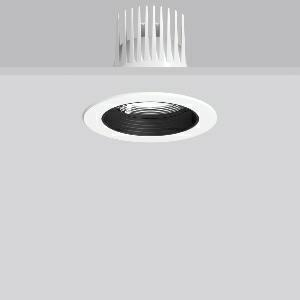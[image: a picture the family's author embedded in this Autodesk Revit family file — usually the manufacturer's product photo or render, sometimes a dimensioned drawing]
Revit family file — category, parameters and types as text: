
# Revit family: heledon_maxi_e_901767_002_2_c0ee
name_source: partatom
category: Lighting Fixtures
units: mm (PartAtom-declared; Revit-internal decimal feet)

## family parameters
Cut with Voids When Loaded = No
Host = Face
Light Source = No
Part Type = Normal
Room Calculation Point = No
Round Connector Dimension = Use Diameter
Shared = No

## types (1)
- HELEDON maxi E (1 x LED Modul 927, 3500 lm, 2700)
    Apparent Load = 35 VA
    Approval mark = CE
    CIE Flux Codes = 97 100 100 100 100
    Color Rendering = 92
    Color Temperature = 2700
    Default Elevation = 1800 mm
    Description = Series: HELEDON maxi
Round recessed downlight. Housing: die-cast aluminium, powder-coated. Black plastic ring and recessed LED to prevent glare from the side. Optical assembly with lens made of plastic (polycarbonate) for the best homogeneous light distribution - can be changed without tools. Best colour rendering index Ra>90. Suitable for Recessed ceiling mounting. Installation without tools thanks to spring fastening system. Including separate LED converter with connecting cable 600 mm.High quality converter without flickering and stroboscopic effect. Through-wiring box (5 pole) available as accessory. The following accessories can be mounted without use of tools: interchangeable lenses, decorative glasses, honeycomb louvre, clear and frosted diffusers, white interchangeable plastic ring. 
Colour: traffic white, matt (RAL 9016)
Diameter: 162 mm
Height: 3 mm
Cut-out diameter: 152 mm
Recess height: 200 mm
Luminaire: recess height: 135 mm
Lamp: LED
Socket: without socket
Colour temperature: 2700K
Colour rendering index (CRI): 92
System power: 35 W
Rated luminous flux: 3500 lm
Luminous efficiency: 100 lm/W
Control gear: Regulated power supply
Protection class: II
Type of protection: IP 20
    Height = 0 mm  [stored 0 ft]
    Lamp = 1 x LED Modul 927
    Lamp Light Flux = 3500 lm
    Lamp count = 1
    Length = 162 mm
    Lifetime = 50000 h
    Luminous efficacy = 100 lm/W
    Manufacturer = RZB
    ModVariant = No
    Model = 901767.002.2
    Mounting Place = Ceiling
    Mounting Type = Recessed
    Number of Poles = 1
    OnlyDefault = Yes
    Power Factor = 1
    Product Name = HELEDON maxi E
    Product group = Recessed downlights
    ProductGroupID = 402
    Protection Class = Protection class II
    Protection Degree = IP 20
    RLX_Detail_Level = 1
    RLX_Emergency_Light_Flux = 0 lm
    RLX_Emergency_Type = 0
    RLX_Emergency_Type_DB = No
    RlxData = <blob elided: 119117 chars, md5=0c7caebb>
    Socket = socket
    Standby Power = 0 W
    System Light Flux = 3500 lm
    System Power = 35 W
    Type Comments = Product without accessories
    Type Image = 901663.002.jpg
    URL = http://relux.com
    VarID = ---
    Voltage = 230 V
    Voltage Range = 220-240 V
    Weight = 0.00 kg
    Width = 0 mm  [stored 0 ft]

note: [stored X ft] marks values corroborated as IEEE doubles in the binary element streams (Revit-internal decimal feet)

## geometry (parser evidence)
native form markers: Blend x4, Sweep x13
no freeform markers — native parametric forms only
